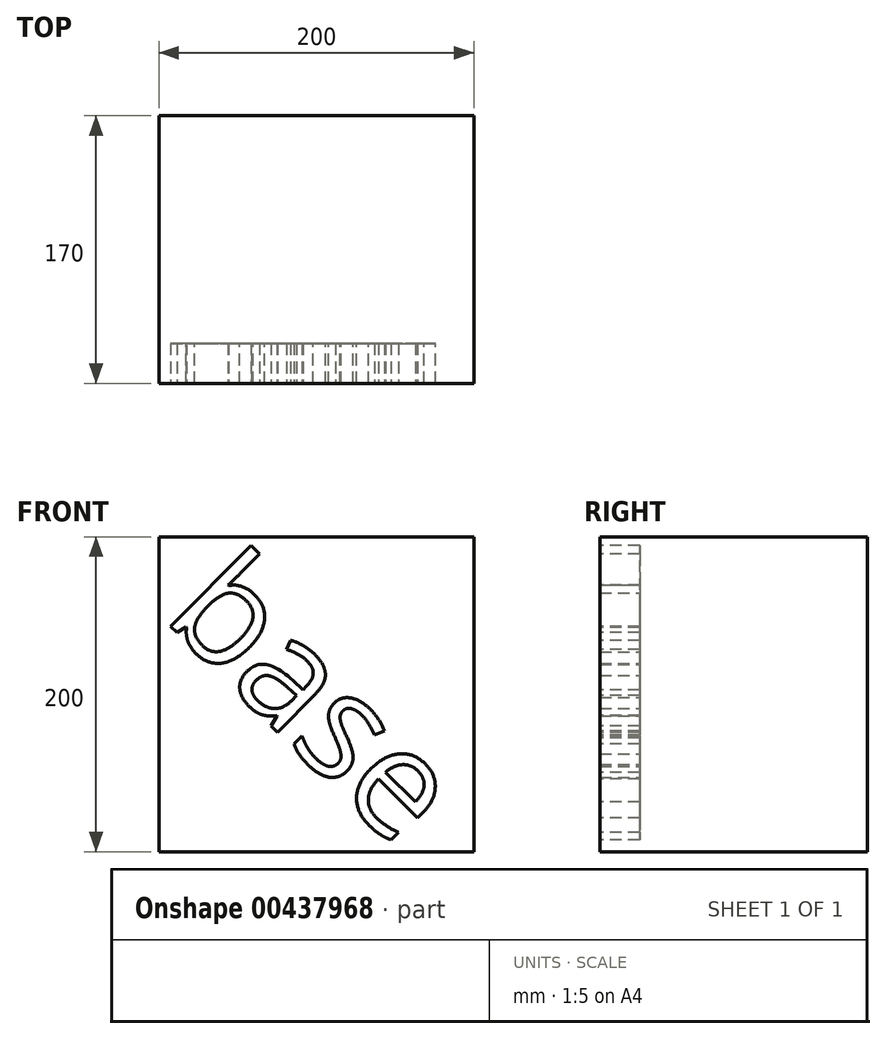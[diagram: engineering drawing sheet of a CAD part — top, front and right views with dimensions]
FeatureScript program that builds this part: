
annotation { "Feature Type Name" : "Feature", "Feature Type Description" : "" }
export const myFeature = defineFeature(function(context is Context, id is Id, definition is map)
    precondition{}
    {
        {
            var Q0;
            Q0=qCreatedBy(makeId("Front.planeOp"),FACE);
            var sketch = newSketch(context, id + "F0", { "sketchPlane" : qUnion([Q0])});
            skLineSegment(sketch, "E0.bottom", {"start": v(-4032.8, -2334.83) * mm, "end": v(-3832.8, -2334.83) * mm});
            skLineSegment(sketch, "E0.top", {"start": v(-4032.8, -2534.83) * mm, "end": v(-3832.8, -2534.83) * mm});
            skLineSegment(sketch, "E0.left", {"start": v(-4032.8, -2334.83) * mm, "end": v(-4032.8, -2534.83) * mm});
            skLineSegment(sketch, "E0.right", {"start": v(-3832.8, -2334.83) * mm, "end": v(-3832.8, -2534.83) * mm});
            skSolve(sketch);
        }
        {
            var Q0;
            Q0=qSketchRegion(id+"F0",true);
            extrude(context, id + "F1", {"entities" : qUnion([Q0]), "depth" : 170 * mm});
        }
        {
            var Q0;
            Q0=makeQuery(id+"F1.opExtrude","CAP_FACE",FACE,{"disambiguationData":[OSD([sQuery(id+"F0.wireOp",EDGE,"E0.bottom"),sQuery(id+"F0.wireOp",EDGE,"E0.top"),sQuery(id+"F0.wireOp",EDGE,"E0.left"),sQuery(id+"F0.wireOp",EDGE,"E0.right")])],"isStart":false});
            var sketch = newSketch(context, id + "F2", { "sketchPlane" : qUnion([Q0])});
            skText(sketch, "E1", { "text": "base", "fontName": "OpenSans-Regular.ttf"});
            const initialGuessF2  = {"E1": [-4.03114, -2.38588, 0.70963, -0.70458, 0.06858]};
            skSetInitialGuess(sketch, initialGuessF2);
            skSolve(sketch);
        }
        {
            var Q0;
            Q0=qSketchRegion(id+"F2",true);
            extrude(context, id + "F3", {"entities" : qUnion([Q0]), "operationType" : NewBodyOperationType.REMOVE, "oppositeDirection" : true, "depth" : 25.4 * mm});
        }
    });
